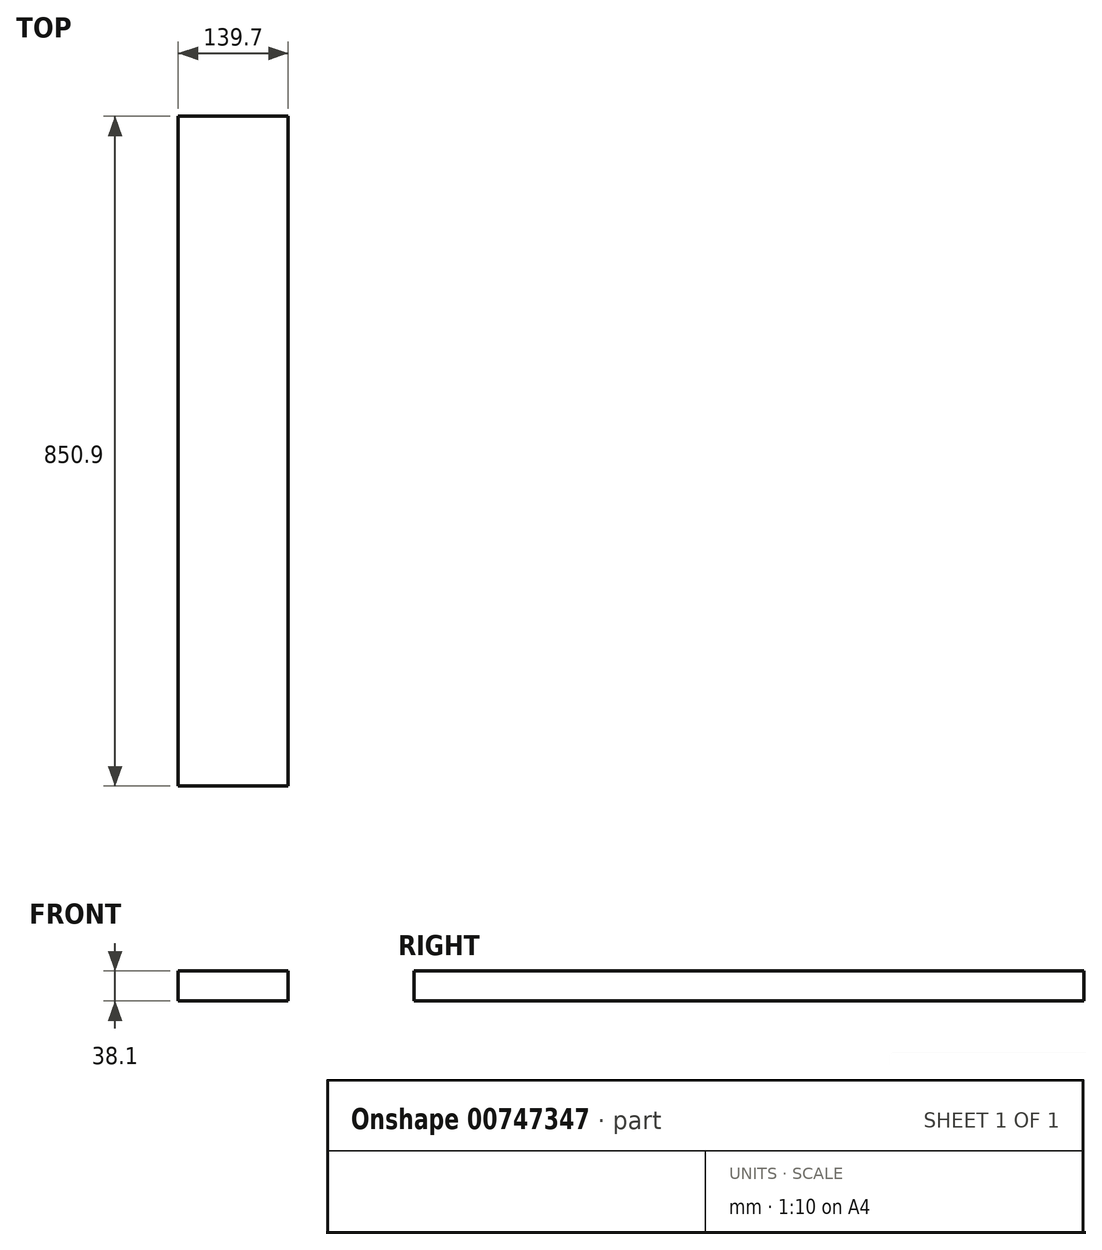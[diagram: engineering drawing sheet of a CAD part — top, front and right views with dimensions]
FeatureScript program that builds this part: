
annotation { "Feature Type Name" : "Feature", "Feature Type Description" : "" }
export const myFeature = defineFeature(function(context is Context, id is Id, definition is map)
    precondition{}
    {
        {
            var Q0;
            Q0=qCreatedBy(makeId("Front.planeOp"),FACE);
            var sketch = newSketch(context, id + "F0", { "sketchPlane" : qUnion([Q0])});
            skLineSegment(sketch, "E0.bottom", {"start": v(0, 0) * mm, "end": v(139.7, 0) * mm});
            skLineSegment(sketch, "E0.top", {"start": v(0, 38.1) * mm, "end": v(139.7, 38.1) * mm});
            skLineSegment(sketch, "E0.left", {"start": v(0, 0) * mm, "end": v(0, 38.1) * mm});
            skLineSegment(sketch, "E0.right", {"start": v(139.7, 0) * mm, "end": v(139.7, 38.1) * mm});
            skSolve(sketch);
        }
        {
            var Q0;
            Q0=qSketchRegion(id+"F0",true);
            extrude(context, id + "F1", {"entities" : qUnion([Q0]), "depth" : 850.9 * mm, "offsetDistance" : 25.4 * mm});
        }
    });
